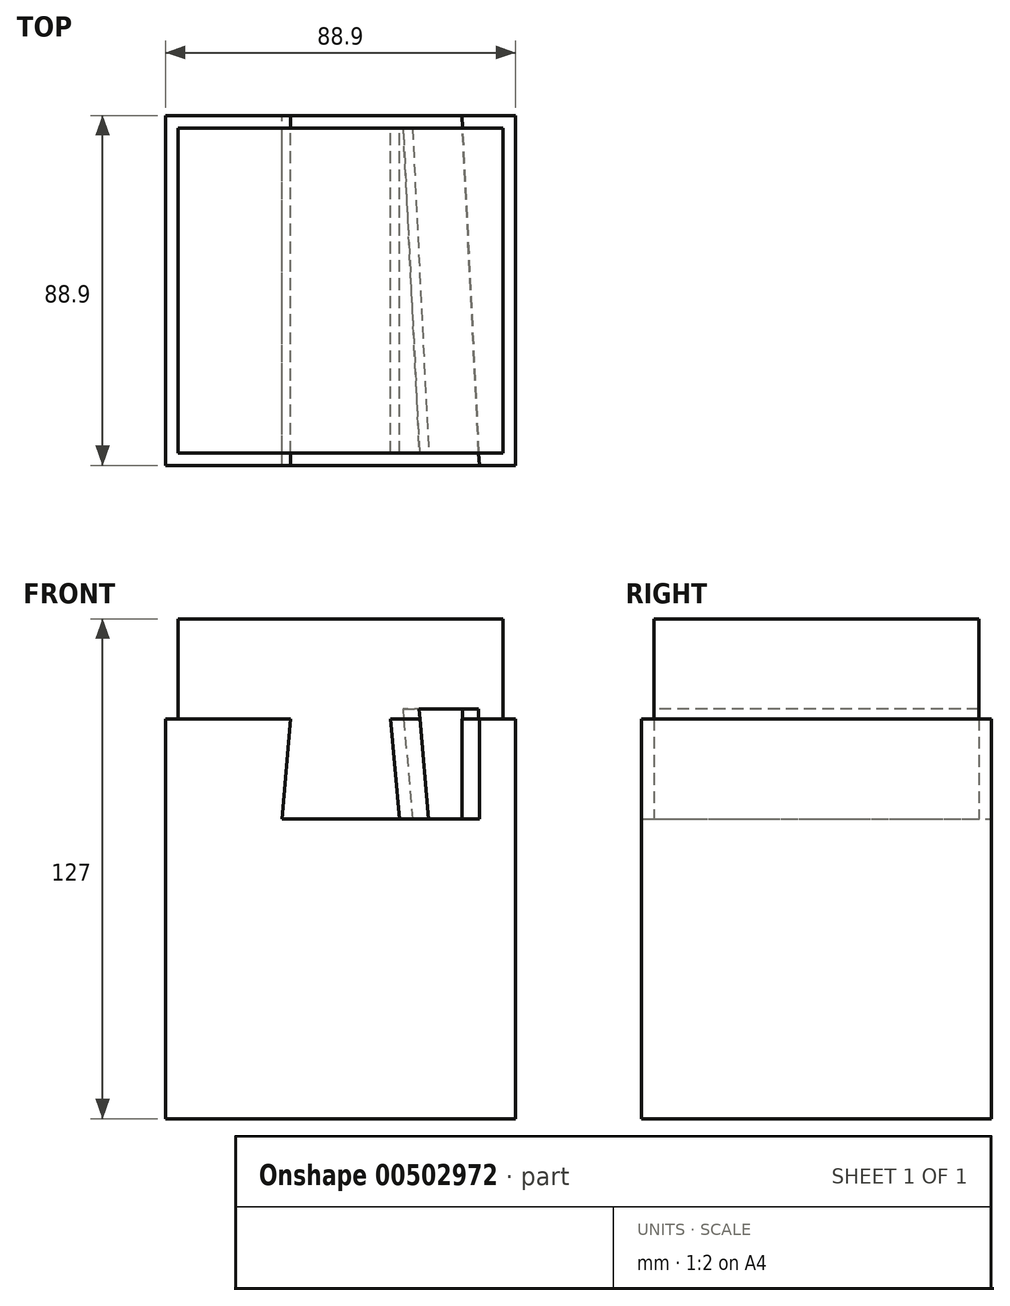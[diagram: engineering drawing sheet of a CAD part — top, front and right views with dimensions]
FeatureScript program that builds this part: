
annotation { "Feature Type Name" : "Feature", "Feature Type Description" : "" }
export const myFeature = defineFeature(function(context is Context, id is Id, definition is map)
    precondition{}
    {
        {
            var Q0;
            Q0=qCreatedBy(makeId("Top.planeOp"),FACE);
            var sketch = newSketch(context, id + "F0", { "sketchPlane" : qUnion([Q0])});
            skLineSegment(sketch, "E0.bottom", {"start": v(44.45, 44.45) * mm, "end": v(-44.45, 44.45) * mm});
            skLineSegment(sketch, "E0.top", {"start": v(44.45, -44.45) * mm, "end": v(-44.45, -44.45) * mm});
            skLineSegment(sketch, "E0.left", {"start": v(44.45, 44.45) * mm, "end": v(44.45, -44.45) * mm});
            skLineSegment(sketch, "E0.right", {"start": v(-44.45, 44.45) * mm, "end": v(-44.45, -44.45) * mm});
            skSolve(sketch);
        }
        {
            var Q0;
            Q0=makeQuery(id+"F0.imprint","IMPRINT",FACE,{"disambiguationData":[TD([[makeQuery(id+"F0.imprint","IMPRINT",EDGE,{"derivedFrom":sQuery(id+"F0.wireOp",EDGE,"E0.bottom")}),1.0]])]});
            extrude(context, id + "F1", {"entities" : qUnion([Q0]), "oppositeDirection" : true, "depth" : 101.6 * mm});
        }
        {
            var Q0;
            Q0=qCreatedBy(makeId("Front.planeOp"),FACE);
            var sketch = newSketch(context, id + "F2", { "sketchPlane" : qUnion([Q0])});
            skLineSegment(sketch, "E1", {"start": v(-12.7, 0) * mm, "end": v(-14.92, -25.4) * mm});
            skLineSegment(sketch, "E2", {"start": v(-14.92, -25.4) * mm, "end": v(10.16, -25.4) * mm});
            skLineSegment(sketch, "E3", {"start": v(10.16, -25.4) * mm, "end": v(10.16, 0) * mm});
            skLineSegment(sketch, "E4", {"start": v(10.16, 0) * mm, "end": v(-12.7, 0) * mm});
            skSolve(sketch);
        }
        {
            var Q0;
            Q0 = qSketchRegion(id + "F2", true);
            extrude(context, id + "F3", {"entities" : qUnion([Q0]), "operationType" : NewBodyOperationType.REMOVE, "endBound" : BoundingType.SYMMETRIC, "depth" : 101.6 * mm});
        }
        {
            var Q0;
            Q0=qCreatedBy(makeId("Top.planeOp"),FACE);
            var sketch = newSketch(context, id + "F4", { "sketchPlane" : qUnion([Q0])});
            skLineSegment(sketch, "E5", {"start": v(15.88, 67.58) * mm, "end": v(15.88, 44.45) * mm});
            skLineSegment(sketch, "E6", {"start": v(15.88, 44.45) * mm, "end": v(-238.12, 31.75) * mm});
            skSolve(sketch);
        }
        {
            var Q0;
            Q0=makeQuery(id+"F1.opExtrude","SWEPT_FACE",FACE,{"disambiguationData":[OSD([sQuery(id+"F0.wireOp",EDGE,"E0.bottom")])]});
            var sketch = newSketch(context, id + "F5", { "sketchPlane" : qUnion([Q0])});
            skLineSegment(sketch, "E7", {"start": v(-15.88, 0) * mm, "end": v(-15.88, 32.24) * mm});
            skSolve(sketch);
        }
        {
            var Q0;
            Q0=sQuery(id+"F5.wireOp",VERTEX,"E7.end");
            var Q1;
            Q1=sQuery(id+"F4.wireOp",VERTEX,"E6.end");
            var Q2;
            Q2=sQuery(id+"F5.wireOp",VERTEX,"E7.start");
            cPlane(context, id + "F6", {"entities" : qUnion([Q0, Q1, Q2]), "cplaneType" : CPlaneType.THREE_POINT, "offset" : 0 * mm, "width" : 152.4 * mm, "height" : 152.4 * mm});
        }
        {
            var Q0;
            Q0=qCreatedBy(id+"F6.planeOp",FACE);
            var sketch = newSketch(context, id + "F7", { "sketchPlane" : qUnion([Q0])});
            skLineSegment(sketch, "E8", {"start": v(-20.3, -25.4) * mm, "end": v(-18.07, 0) * mm});
            skLineSegment(sketch, "E9", {"start": v(-18.07, 0) * mm, "end": v(-0.3, 0) * mm});
            skLineSegment(sketch, "E10", {"start": v(-0.3, 0) * mm, "end": v(-0.3, -25.4) * mm});
            skLineSegment(sketch, "E11", {"start": v(-0.3, -25.4) * mm, "end": v(-20.3, -25.4) * mm});
            skSolve(sketch);
        }
        {
            var Q0;
            Q0 = qSketchRegion(id + "F7", true);
            extrude(context, id + "F8", {"entities" : qUnion([Q0]), "operationType" : NewBodyOperationType.REMOVE, "endBound" : BoundingType.SYMMETRIC, "oppositeDirection" : true, "depth" : 203.2 * mm});
        }
        {
            var Q0;
            Q0=qCreatedBy(makeId("Front.planeOp"),FACE);
            var sketch = newSketch(context, id + "F9", { "sketchPlane" : qUnion([Q0])});
            skLineSegment(sketch, "E12", {"start": v(41.28, 25.4) * mm, "end": v(-41.28, 25.4) * mm});
            skLineSegment(sketch, "E13", {"start": v(-41.28, 25.4) * mm, "end": v(-41.28, 0) * mm});
            skLineSegment(sketch, "E14", {"start": v(-41.28, 0) * mm, "end": v(-12.7, 0) * mm});
            skLineSegment(sketch, "E15", {"start": v(-12.7, 0) * mm, "end": v(-14.92, -25.4) * mm});
            skLineSegment(sketch, "E16", {"start": v(-14.92, -25.4) * mm, "end": v(14.92, -25.4) * mm});
            skLineSegment(sketch, "E17", {"start": v(14.92, -25.4) * mm, "end": v(12.7, 0) * mm});
            skLineSegment(sketch, "E18", {"start": v(12.7, 0) * mm, "end": v(41.28, 0) * mm});
            skLineSegment(sketch, "E19", {"start": v(41.28, 0) * mm, "end": v(41.28, 25.4) * mm});
            skSolve(sketch);
        }
        {
            var Q0;
            Q0=makeQuery(id+"F9.imprint","IMPRINT",FACE,{"disambiguationData":[TD([[makeQuery(id+"F9.imprint","IMPRINT",EDGE,{"derivedFrom":sQuery(id+"F9.wireOp",EDGE,"E12")}),1.0]])]});
            extrude(context, id + "F10", {"entities" : qUnion([Q0]), "endBound" : BoundingType.SYMMETRIC, "depth" : 82.55 * mm});
        }
        {
            var Q0;
            Q0=qCreatedBy(makeId("Front.planeOp"),FACE);
            var sketch = newSketch(context, id + "F11", { "sketchPlane" : qUnion([Q0])});
            skLineSegment(sketch, "E20", {"start": v(12.7, 0) * mm, "end": v(14.92, -25.4) * mm});
            skLineSegment(sketch, "E21", {"start": v(14.92, -25.4) * mm, "end": v(25.08, -25.4) * mm});
            skLineSegment(sketch, "E22", {"start": v(25.08, -25.4) * mm, "end": v(25.08, 0) * mm});
            skLineSegment(sketch, "E23", {"start": v(25.08, 0) * mm, "end": v(12.7, 0) * mm});
            skSolve(sketch);
        }
        {
            var Q0;
            Q0 = qSketchRegion(id + "F11", true);
            extrude(context, id + "F12", {"entities" : qUnion([Q0]), "endBound" : BoundingType.SYMMETRIC, "depth" : 82.55 * mm});
        }
        {
            var Q0;
            Q0=qCreatedBy(id+"F6.planeOp",FACE);
            var sketch = newSketch(context, id + "F13", { "sketchPlane" : qUnion([Q0])});
            skLineSegment(sketch, "E24", {"start": v(-17.85, 2.54) * mm, "end": v(-20.3, -25.4) * mm});
            skLineSegment(sketch, "E25", {"start": v(-20.3, -25.4) * mm, "end": v(-33, -25.4) * mm});
            skLineSegment(sketch, "E26", {"start": v(-33, -25.4) * mm, "end": v(-33, 2.54) * mm});
            skLineSegment(sketch, "E27", {"start": v(-33, 2.54) * mm, "end": v(-17.85, 2.54) * mm});
            skSolve(sketch);
        }
        {
            var Q0;
            Q0 = qSketchRegion(id + "F13", true);
            extrude(context, id + "F14", {"entities" : qUnion([Q0]), "operationType" : NewBodyOperationType.REMOVE, "endBound" : BoundingType.SYMMETRIC, "depth" : 203.2 * mm});
        }
    });
